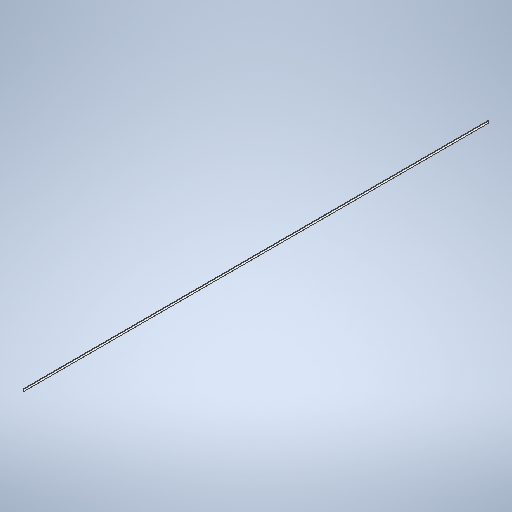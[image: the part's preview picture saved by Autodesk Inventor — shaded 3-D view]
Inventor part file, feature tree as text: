
AUTODESK INVENTOR PART (.ipt)
format: ipt  version: 2025 (Build 290162010, 162A)  size: 253,440 bytes
history: native  units: in
note: dims shown in document units (in); Inventor stores cm internally (conversion verified against a paired STEP export)
features: extrude x1, sketch x1
ambient origin geometry x8: Origin, YZ Plane, XZ Plane, XY Plane, X Axis, Y Axis, Z Axis, Center Point
bodies: Solid1 (feature_tree)
feature tree (2):
  extrude  "Extrusion1"  Depth=0.3125in TaperAngle=0.0deg
  sketch  "Sketch1"  dims[d1=1.25in d2=0.3125in d3=0.0in d4=289.0in]
